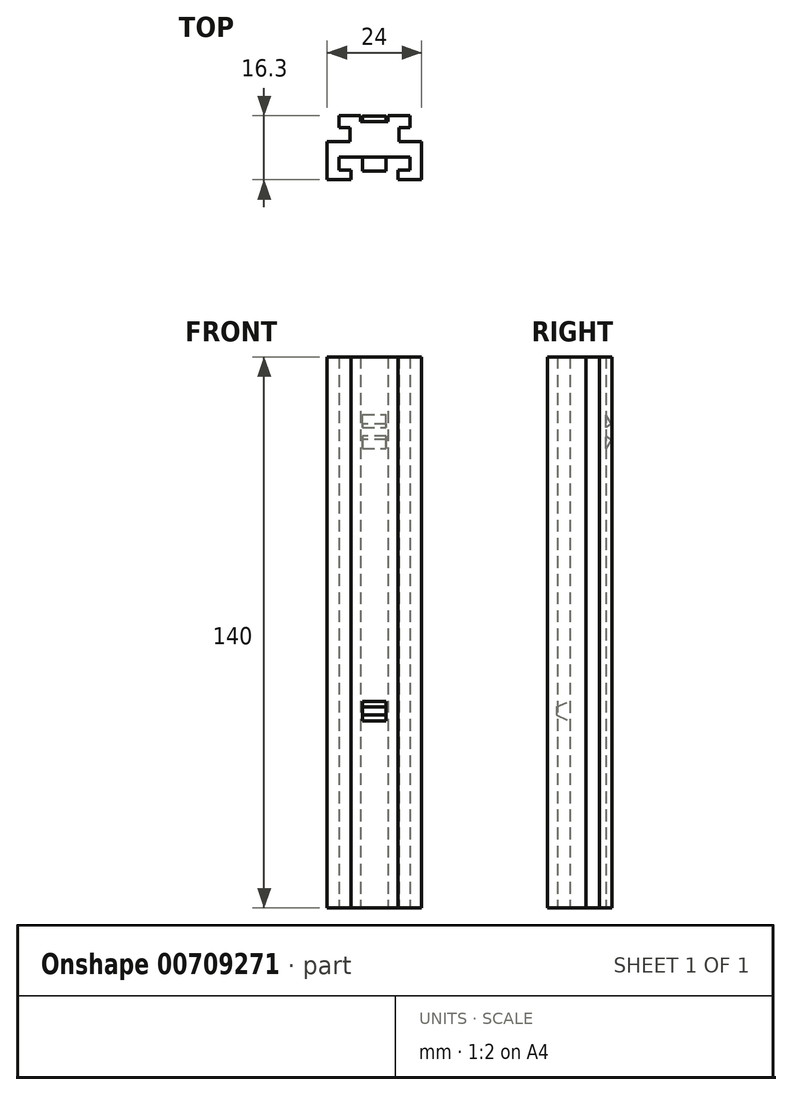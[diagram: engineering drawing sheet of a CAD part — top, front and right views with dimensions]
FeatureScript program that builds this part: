
annotation { "Feature Type Name" : "Feature", "Feature Type Description" : "" }
export const myFeature = defineFeature(function(context is Context, id is Id, definition is map)
    precondition{}
    {
        {
            var Q0;
            Q0=qCreatedBy(makeId("Top.planeOp"),FACE);
            var sketch = newSketch(context, id + "F0", { "sketchPlane" : qUnion([Q0])});
            skLineSegment(sketch, "E0", {"start": v(0, 0) * mm, "end": v(9, 0) * mm});
            skLineSegment(sketch, "E1", {"start": v(9, 0) * mm, "end": v(9, -3.2) * mm});
            skLineSegment(sketch, "E2", {"start": v(9, -3.2) * mm, "end": v(6, -3.2) * mm});
            skLineSegment(sketch, "E3", {"start": v(6, -3.2) * mm, "end": v(6, -5.7) * mm});
            skLineSegment(sketch, "E4", {"start": v(6, -5.7) * mm, "end": v(12, -5.7) * mm});
            skLineSegment(sketch, "E5", {"start": v(12, -5.7) * mm, "end": v(12, 4) * mm});
            skLineSegment(sketch, "E6", {"start": v(12, 4) * mm, "end": v(6.25, 4) * mm});
            skLineSegment(sketch, "E7", {"start": v(6.25, 4) * mm, "end": v(6.25, 7.5) * mm});
            skLineSegment(sketch, "E8", {"start": v(6.25, 7.5) * mm, "end": v(9, 7.5) * mm});
            skLineSegment(sketch, "E9", {"start": v(9, 7.5) * mm, "end": v(9, 10.6) * mm});
            skLineSegment(sketch, "E10", {"start": v(9, 10.6) * mm, "end": v(3.5, 10.6) * mm});
            skLineSegment(sketch, "E11", {"start": v(3.5, 10.6) * mm, "end": v(3.5, 9.1) * mm});
            skLineSegment(sketch, "E12", {"start": v(3.5, 9.1) * mm, "end": v(0, 9.1) * mm});
            skLineSegment(sketch, "E13.MirrorCS", {"start": v(-3.5, 10.6) * mm, "end": v(-3.5, 9.1) * mm});
            skLineSegment(sketch, "E14.MirrorCS", {"start": v(-9, 0) * mm, "end": v(-9, -3.2) * mm});
            skLineSegment(sketch, "E15.MirrorCS", {"start": v(-6.25, 7.5) * mm, "end": v(-9, 7.5) * mm});
            skLineSegment(sketch, "E16.MirrorCS", {"start": v(-12, 4) * mm, "end": v(-6.25, 4) * mm});
            skLineSegment(sketch, "E17.MirrorCS", {"start": v(-6, -5.7) * mm, "end": v(-12, -5.7) * mm});
            skLineSegment(sketch, "E18.MirrorCS", {"start": v(-9, 10.6) * mm, "end": v(-3.5, 10.6) * mm});
            skLineSegment(sketch, "E19.MirrorCS", {"start": v(-9, 7.5) * mm, "end": v(-9, 10.6) * mm});
            skLineSegment(sketch, "E20.MirrorCS", {"start": v(-6.25, 4) * mm, "end": v(-6.25, 7.5) * mm});
            skLineSegment(sketch, "E21.MirrorCS", {"start": v(-12, -5.7) * mm, "end": v(-12, 4) * mm});
            skLineSegment(sketch, "E22.MirrorCS", {"start": v(-9, -3.2) * mm, "end": v(-6, -3.2) * mm});
            skLineSegment(sketch, "E23.MirrorCS", {"start": v(-6, -3.2) * mm, "end": v(-6, -5.7) * mm});
            skLineSegment(sketch, "E24.MirrorCS", {"start": v(0, 0) * mm, "end": v(-9, 0) * mm});
            skLineSegment(sketch, "E25.MirrorCS", {"start": v(-3.5, 9.1) * mm, "end": v(0, 9.1) * mm});
            skSolve(sketch);
        }
        {
            var Q0;
            Q0=makeQuery(id+"F0.imprint","IMPRINT",FACE,{"disambiguationData":[TD([[makeQuery(id+"F0.imprint","IMPRINT",EDGE,{"derivedFrom":sQuery(id+"F0.wireOp",EDGE,"E0")}),1.0]])]});
            extrude(context, id + "F1", {"entities" : qUnion([Q0]), "depth" : 140 * mm, "offsetDistance" : 25 * mm});
        }
        {
            var Q0;
            Q0=qCreatedBy(makeId("Right.planeOp"),FACE);
            var sketch = newSketch(context, id + "F2", { "sketchPlane" : qUnion([Q0])});
            skLineSegment(sketch, "E26", {"start": v(-3.5, 51) * mm, "end": v(0, 52.5) * mm});
            skLineSegment(sketch, "E27", {"start": v(0, 52.5) * mm, "end": v(0, 47.5) * mm});
            skLineSegment(sketch, "E28", {"start": v(-3.5, 51) * mm, "end": v(-3.5, 49) * mm});
            skLineSegment(sketch, "E29", {"start": v(-3.5, 49) * mm, "end": v(0, 47.5) * mm});
            skSolve(sketch);
        }
        {
            var Q0;
            Q0=makeQuery(id+"F2.imprint","IMPRINT",FACE,{"disambiguationData":[TD([[makeQuery(id+"F2.imprint","IMPRINT",EDGE,{"derivedFrom":sQuery(id+"F2.wireOp",EDGE,"E26")}),-1.0]])]});
            extrude(context, id + "F3", {"entities" : qUnion([Q0]), "operationType" : NewBodyOperationType.ADD, "depth" : 3 * mm, "offsetDistance" : 25 * mm, "hasSecondDirection" : true, "secondDirectionOppositeDirection" : true, "secondDirectionDepth" : 3 * mm});
        }
        {
            var Q0;
            Q0=qCreatedBy(makeId("Right.planeOp"),FACE);
            var sketch = newSketch(context, id + "F4", { "sketchPlane" : qUnion([Q0])});
            skLineSegment(sketch, "E30", {"start": v(7.5, 114) * mm, "end": v(7.5, 128) * mm});
            skLineSegment(sketch, "E31", {"start": v(10.5, 123) * mm, "end": v(7.5, 128) * mm});
            skLineSegment(sketch, "E32", {"start": v(10.5, 123) * mm, "end": v(9, 122) * mm});
            skLineSegment(sketch, "E33", {"start": v(9, 122) * mm, "end": v(9, 120) * mm});
            skLineSegment(sketch, "E34", {"start": v(9, 120) * mm, "end": v(10.5, 119) * mm});
            skLineSegment(sketch, "E35", {"start": v(10.5, 119) * mm, "end": v(7.5, 114) * mm});
            skSolve(sketch);
        }
        {
            var Q0;
            Q0 = qSketchRegion(id + "F4", true);
            extrude(context, id + "F5", {"entities" : qUnion([Q0]), "operationType" : NewBodyOperationType.ADD, "depth" : 3 * mm, "offsetDistance" : 25 * mm, "hasSecondDirection" : true, "secondDirectionOppositeDirection" : true, "secondDirectionDepth" : 3 * mm});
        }
    });
